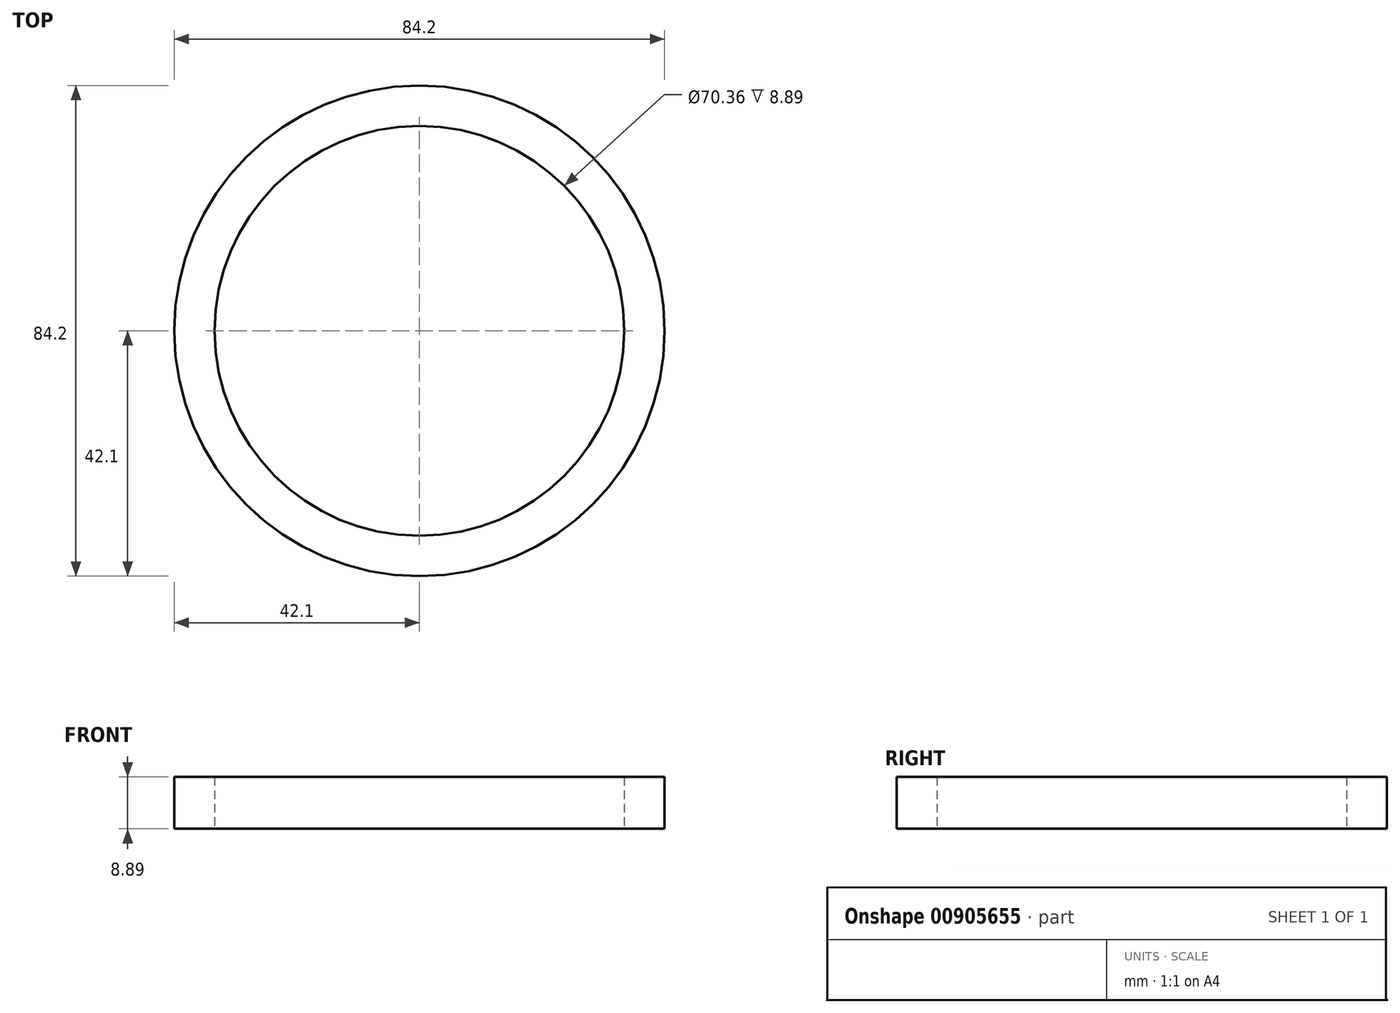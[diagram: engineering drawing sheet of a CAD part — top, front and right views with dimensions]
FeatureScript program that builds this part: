
annotation { "Feature Type Name" : "Feature", "Feature Type Description" : "" }
export const myFeature = defineFeature(function(context is Context, id is Id, definition is map)
    precondition{}
    {
        {
            var Q0;
            Q0=qCreatedBy(makeId("Top.planeOp"),FACE);
            var sketch = newSketch(context, id + "F0", { "sketchPlane" : qUnion([Q0])});
            skCircle(sketch, "E0", {"center": v(0, 0) * mm, "radius": 35.18 * mm});
            skCircle(sketch, "E1", {"center": v(0, 0) * mm, "radius": 42.1 * mm});
            skSolve(sketch);
        }
        {
            var Q0;
            Q0=makeQuery(id+"F0.imprint","IMPRINT",FACE,{"disambiguationData":[TD([[makeQuery(id+"F0.imprint","IMPRINT",EDGE,{"derivedFrom":sQuery(id+"F0.wireOp",EDGE,"E0")}),-1.0]])]});
            extrude(context, id + "F1", {"entities" : qUnion([Q0]), "depth" : 8.9 * mm, "offsetDistance" : 25.4 * mm});
        }
    });
